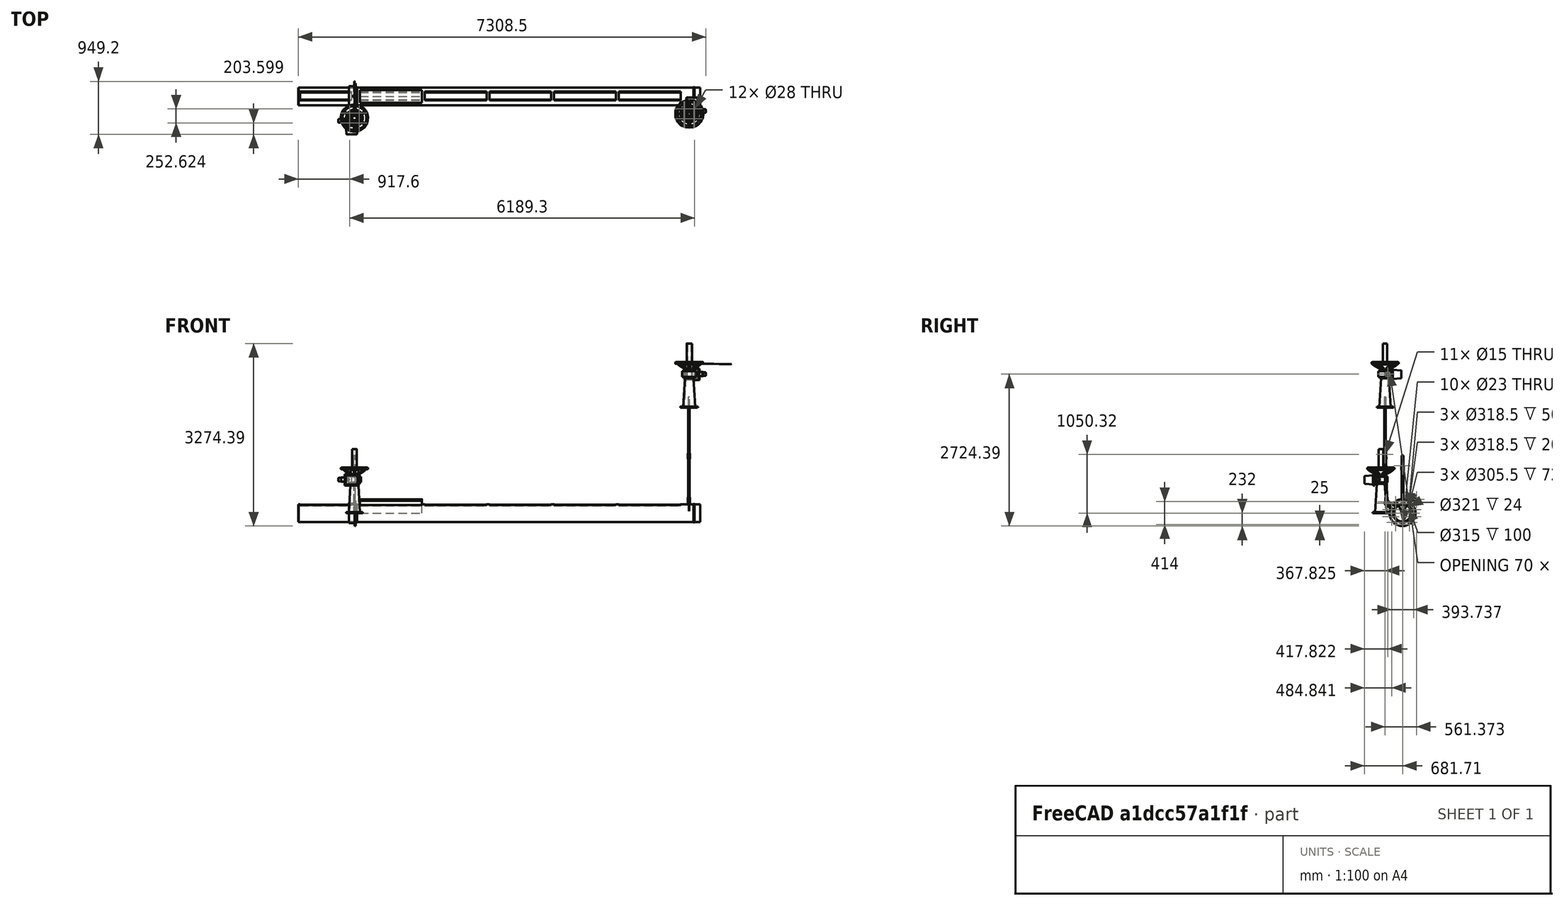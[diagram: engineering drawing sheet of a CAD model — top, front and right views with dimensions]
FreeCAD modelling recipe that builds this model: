
FCSTD DOCUMENT  (FreeCAD 0.21R33771 (Git))
Label: pipeSkimmer2
License: All rights reserved
LicenseURL: https://en.wikipedia.org/wiki/All_rights_reserved
objects: Part::Extrusion×9, Sketcher::SketchObject×9, App::FeaturePython×8, Part::FeaturePython×7, App::Part×7, Part::Compound×4, Part::Cut×3, Part::Revolution×1, Spreadsheet::Sheet×1, Part::Feature×1, Part::Cylinder×1
note: 34 computed .brp shape members not serialized (recipe doc carries the construction recipe); baked Part::Feature solids carry a one-line shape summary decoded from their .brp

FEATURE [Part::FeaturePython] Flange  # WARN: FeaturePython — macro-defined, semantics opaque (R4)
  Placement = pos=(0,0,0) rot=(0.57735,0.57735,0.57735;2.0944rad)
  dia = 6
  fittings = 00_Flange
  material = 0
  standard = 1
FEATURE [Part::FeaturePython] Ring  # WARN: FeaturePython — macro-defined, semantics opaque (R4)
  D = 360
  Placement = pos=(0,0,0) rot=(0,1,0;1.5708rad)
  d = 315
  sface = 0
FEATURE [Part::Extrusion] Extrude
  Base = -> Ring
  Dir = (1,0,0)
  DirMode = 2
  FaceMakerClass = Part::FaceMakerBullseye
  LengthFwd = 100
  LengthRev = 0
  Reversed = true
  Solid = true
  Symmetric = false
FEATURE [App::Part] Part  label="brg01"
  Group = -> [Ring,Extrude,Flange]
  Origin = -> Origin
  Placement = pos=(6200,-1.1983e-12,0) rot=(0,0,1;0rad)
  expr: .Placement.Base.x = Spreadsheet.L0 - Spreadsheet.l1 + Spreadsheet.l1 - 300
FEATURE [Part::FeaturePython] Straight_tube  # WARN: FeaturePython — macro-defined, semantics opaque (R4)
  L = 7200
  Placement = pos=(-1000,0,0) rot=(0,0,1;0rad)
  dia = 16
  fittings = 05_Straight pipe
  material = 1
  standard = 1
  expr: .Placement.Base.x = -Spreadsheet.l1
  expr: L = Spreadsheet.L0 + Spreadsheet.l1 - 300
FEATURE [Sketcher::SketchObject] Sketch
  FullyConstrained = true
  Placement = pos=(0,0,0) rot=(1,0,0;1.5708rad)
  expr: Constraints[35] = Spreadsheet.L0 - 400
  sketch-geometry (12):
    g0: LineSegment StartX=6080 StartY=159.25 StartZ=0 EndX=6100 EndY=159.25 EndZ=0
    g1: LineSegment StartX=6100 StartY=159.25 StartZ=0 EndX=6100 EndY=164.25 EndZ=0
    g2: LineSegment StartX=6100 StartY=164.25 StartZ=0 EndX=6080 EndY=164.25 EndZ=0
    g3: LineSegment StartX=6080 StartY=164.25 StartZ=0 EndX=6080 EndY=159.25 EndZ=0
    g4: LineSegment StartX=0 StartY=159.25 StartZ=0 EndX=0 EndY=169.25 EndZ=0
    g5: LineSegment StartX=0 StartY=169.25 StartZ=0 EndX=19 EndY=169.25 EndZ=0
    g6: LineSegment StartX=19 StartY=169.25 StartZ=0 EndX=19 EndY=164.25 EndZ=0
    g7: LineSegment StartX=19 StartY=164.25 StartZ=0 EndX=31 EndY=164.25 EndZ=0
    g8: LineSegment StartX=31 StartY=164.25 StartZ=0 EndX=31 EndY=169.25 EndZ=0
    g9: LineSegment StartX=31 StartY=169.25 StartZ=0 EndX=50 EndY=169.25 EndZ=0
    g10: LineSegment StartX=50 StartY=169.25 StartZ=0 EndX=50 EndY=159.25 EndZ=0
    g11: LineSegment StartX=50 StartY=159.25 StartZ=0 EndX=0 EndY=159.25 EndZ=0
  constraints (36):
    c: Coincident(g0,g1)
    c: Coincident(g1,g2)
    c: Coincident(g2,g3)
    c: Coincident(g3,g0)
    c: Horizontal(g0)
    c: Horizontal(g2)
    c: Vertical(g1)
    c: Vertical(g3)
    c: DistanceY(g-1,g0) = 159.25
    c: DistanceY(g1,g1) = 5
    c: DistanceX(g2,g2) = 20
    c: Vertical(g4)
    c: Coincident(g4,g5)
    c: Horizontal(g5)
    c: Coincident(g5,g6)
    c: Vertical(g6)
    c: Coincident(g6,g7)
    c: Coincident(g7,g8)
    c: Coincident(g8,g9)
    c: Coincident(g9,g10)
    c: Coincident(g10,g11)
    c: Coincident(g11,g4)
    c: Horizontal(g11)
    c: Vertical(g10)
    c: Horizontal(g7)
    c: Horizontal(g9)
    c: Vertical(g8)
    c: DistanceY(g10,g10) = 10
    c: DistanceY(g7,g8) = 5
    c: Horizontal(g8,g5)
    c: DistanceX(g11,g11) = 50
    c: DistanceX(g7,g7) = 12
    c: DistanceX(g5,g5) = 19
    c: DistanceY(g-1,g4) = 159.25
    c: Vertical(g-1,g4)
    c: DistanceX(g-1,g0) = 6100
FEATURE [Part::Revolution] Revolve
  Angle = 360
  Axis = (1,0,0)
  Base = (0,0,0)
  FaceMakerClass = Part::FaceMakerBullseye
  Solid = true
  Source = -> Sketch
  Symmetric = false
FEATURE [Spreadsheet::Sheet] Spreadsheet  label="Spreadsheet_pipeSkimmer"
  cells = A2='tankDia  D0; B2(D0)=13000; A3='fullLength L0; B3(L0)=6500; A4='length       l1; B4(l1)=1000; A5='越流堰数 n0; B5(n0)=5; A6='越流堰長 l3; B6(l3)=1110; A7='開閉台  h2; B7(h2)=1500; A8='開閉台 位置 l2; B8(l2)=500
FEATURE [Sketcher::SketchObject] Sketch001
  FullyConstrained = false
  Placement = pos=(0,0,0) rot=(0.57735,0.57735,0.57735;2.0944rad)
  sketch-geometry (3):
    g0: LineSegment StartX=0 StartY=0 StartZ=0 EndX=114.659 EndY=220.257 EndZ=0
    g1: LineSegment StartX=0 StartY=0 StartZ=0 EndX=-114.659 EndY=220.257 EndZ=0
    g2: ArcOfCircle CenterX=0 CenterY=0 CenterZ=0 NormalX=0 NormalY=0 NormalZ=1 AngleXU=0 Radius=248.314 StartAngle=1.09083 EndAngle=2.05076
  constraints (7):
    c: Coincident(g-1,g0)
    c: Coincident(g1,g0)
    c: Coincident(g2,g0)
    c: Coincident(g2,g1)
    c: Coincident(g2,g0)
    c: Angle(g0,g-2) = 0.479966
    c: Angle(g0,g1) = 0.959931
FEATURE [Part::Extrusion] Extrude001
  Base = -> Sketch001
  Dir = (1,0,0)
  DirMode = 2
  FaceMakerClass = Part::FaceMakerBullseye
  LengthFwd = 1110
  LengthRev = 0
  Placement = pos=(100,0,0) rot=(0,0,1;0rad)
  Solid = true
  Symmetric = false
  expr: LengthFwd = Spreadsheet.l3
FEATURE [Part::FeaturePython] Array  # Draft array (typed FeaturePython)
  AlwaysSyncPlacement = false
  Angle = 360
  ArrayType = 0
  Axis = (0,0,1)
  Base = -> Extrude001
  Center = (0,0,0)
  Count = 5
  ExpandArray = false
  Fuse = false
  IntervalAxis = (0,0,0)
  IntervalX = (1160,0,0)
  IntervalY = (0,100,0)
  IntervalZ = (0,0,100)
  NumberCircles = 3
  NumberPolar = 5
  NumberX = 5
  NumberY = 1
  NumberZ = 1
  PlacementList = 5 placements: arithmetic series from (100,0,0) step (1160,0,0) to (4740,0,0)
  RadialDistance = 50
  ScaleList = (5) [(1,1,1),(1,1,1),(1,1,1),(1,1,1),(1,1,1)]
  Symmetry = 1
  TangentialDistance = 25
  expr: .IntervalX.x = Spreadsheet.l3 + 50
  expr: NumberX = Spreadsheet.n0
FEATURE [Part::Cut] Cut
  Base = -> Straight_tube
  Tool = -> Array
FEATURE [Sketcher::SketchObject] Sketch002
  FullyConstrained = false
  Placement = pos=(-30,0,0) rot=(0.57735,0.57735,0.57735;2.0944rad)
  expr: .Placement.Base.x = -30
  sketch-geometry (3):
    g0: LineSegment StartX=0 StartY=0 StartZ=0 EndX=-124.513 EndY=239.188 EndZ=0
    g1: LineSegment StartX=0 StartY=0 StartZ=0 EndX=124.513 EndY=239.188 EndZ=0
    g2: ArcOfCircle CenterX=0 CenterY=0 CenterZ=0 NormalX=0 NormalY=0 NormalZ=1 AngleXU=0 Radius=269.656 StartAngle=1.09083 EndAngle=2.05076
  constraints (7):
    c: Coincident(g0,g-1)
    c: Coincident(g1,g0)
    c: Coincident(g2,g1)
    c: Coincident(g2,g0)
    c: Coincident(g2,g0)
    c: Angle(g1,g0) = 0.959931
    c: Angle(g1,g-2) = 0.479966
FEATURE [Part::Extrusion] Extrude002
  Base = -> Sketch002
  Dir = (1,0,0)
  DirMode = 2
  FaceMakerClass = Part::FaceMakerBullseye
  LengthFwd = 920
  LengthRev = 0
  Placement = pos=(-25,0,0) rot=(0,0,1;0rad)
  Reversed = true
  Solid = true
  Symmetric = false
  expr: LengthFwd = Spreadsheet.l1 - 80
FEATURE [Part::Cut] Cut001
  Base = -> Cut
  Tool = -> Extrude002
FEATURE [Sketcher::SketchObject] Sketch004
  FullyConstrained = true
  Placement = pos=(0,0,0) rot=(0.57735,0.57735,0.57735;2.0944rad)
  sketch-geometry (6):
    g0: LineSegment StartX=0 StartY=0 StartZ=0 EndX=247.487 EndY=247.487 EndZ=0
    g1: Circle CenterX=247.487 CenterY=247.487 CenterZ=0 NormalX=0 NormalY=0 NormalZ=1 AngleXU=0 Radius=7.5
    g2: ArcOfCircle CenterX=247.487 CenterY=247.487 CenterZ=0 NormalX=0 NormalY=0 NormalZ=1 AngleXU=0 Radius=20 StartAngle=5.62869 EndAngle=8.50848
    g3: LineSegment StartX=235.312 StartY=263.354 StartZ=0 EndX=74.8903 EndY=140.258 EndZ=0
    g4: LineSegment StartX=263.354 StartY=235.312 StartZ=0 EndX=140.258 EndY=74.8903 EndZ=0
    g5: ArcOfCircle CenterX=0 CenterY=0 CenterZ=0 NormalX=0 NormalY=0 NormalZ=1 AngleXU=0 Radius=159 StartAngle=0.490434 EndAngle=1.08036
  constraints (15):
    c: Coincident(g0,g-1)
    c: Angle(g-1,g0) = 0.785398
    c: Coincident(g1,g0)
    c: Radius(g1) = 7.5
    c: Coincident(g2,g1)
    c: Coincident(g5,g3)
    c: Coincident(g5,g4)
    c: Coincident(g5,g0)
    c: Tangent(g2,g3) = -1.5708
    c: Tangent(g2,g4) = 1.5708
    c: Equal(g4,g3)
    c: Radius(g5) = 159
    c: Angle(g3,g4) = 0.261799
    c: Distance(g5,g1) = 350
    c: Radius(g2) = 20
FEATURE [Part::Extrusion] Extrude004
  Base = -> Sketch004
  Dir = (1,0,0)
  DirMode = 2
  FaceMakerClass = Part::FaceMakerBullseye
  LengthFwd = 6
  LengthRev = 0
  Solid = true
  Symmetric = true
FEATURE [App::Part] Part003  label="arm"
  Group = -> [Sketch004,Extrude004]
  Origin = -> Origin003
  Placement = pos=(6000,0,0) rot=(1,0,0;1.8326rad)
  expr: .Placement.Base.x = Spreadsheet.L0 - Spreadsheet.l2
FEATURE [Sketcher::SketchObject] Sketch005
  ExternalGeometry = -> [Cut001]
  FullyConstrained = true
  MapMode = 5
  Placement = pos=(-1000,0,0) rot=(0.57735,-0.57735,-0.57735;2.0944rad)
  expr: .Placement.Base.x = -Spreadsheet.l1
  sketch-geometry (1):
    g0: Circle CenterX=0 CenterY=0 CenterZ=0 NormalX=0 NormalY=0 NormalZ=1 AngleXU=0 Radius=159.25
  constraints (2):
    c: Coincident(g0,g-1)
    c: Equal(g0,g-3)
FEATURE [Part::Extrusion] Extrude005
  Base = -> Sketch005
  Dir = (-1,0,0)
  DirMode = 2
  FaceMakerClass = Part::FaceMakerBullseye
  LengthFwd = 6
  LengthRev = 0
  Solid = true
  Symmetric = false
FEATURE [App::Part] Part001  label="pipe"
  Group = -> [Sketch,Revolve,Cut,Cut001,Sketch002,Sketch001,Straight_tube,Array,Extrude002,Extrude001,Sketch005,Extrude005,Part003]
  Origin = -> Origin001
FEATURE [Part::Feature] Part__Feature  label="電動トップハンドル_LTKD-01 v5"
  Placement = pos=(0,-389.711,-5.7e-14) rot=(1,0,0;1.5708rad)
  shape: bbox 555.2 x 557.2 x 1150 mm, 73 faces (baked)
FEATURE [App::Part] Part004  label="開閉台"
  Group = -> [Part__Feature]
  Origin = -> Origin004
  Placement = pos=(0,-400,1500) rot=(0,0,1;3.14159rad)
  expr: .Placement.Base.z = Spreadsheet.h2
FEATURE [Sketcher::SketchObject] Sketch006
  FullyConstrained = false
  Placement = pos=(0,0,0) rot=(0.57735,0.57735,0.57735;2.0944rad)
  sketch-geometry (5):
    g0: Circle CenterX=0 CenterY=0 CenterZ=0 NormalX=0 NormalY=0 NormalZ=1 AngleXU=0 Radius=7.5
    g1: ArcOfCircle CenterX=0 CenterY=0 CenterZ=0 NormalX=0 NormalY=0 NormalZ=1 AngleXU=0 Radius=20 StartAngle=3.14159 EndAngle=6.28319
    g2: LineSegment StartX=-20 StartY=9.32106e-06 StartZ=0 EndX=-20 EndY=80 EndZ=0
    g3: LineSegment StartX=-20 StartY=80 StartZ=0 EndX=20 EndY=80 EndZ=0
    g4: LineSegment StartX=20 StartY=80 StartZ=0 EndX=20 EndY=3.56439e-05 EndZ=0
  constraints (13):
    c: Coincident(g0,g-1)
    c: Coincident(g1,g0)
    c: Radius(g1) = 20
    c: Radius(g0) = 7.5
    c: Vertical(g2)
    c: Coincident(g2,g3)
    c: Horizontal(g3)
    c: Coincident(g3,g4)
    c: Vertical(g4)
    c: Coincident(g1,g4)
    c: Coincident(g1,g2)
    c: DistanceY(g-1,g3) = 80
    c: DistanceX(g3,g3) = 40
FEATURE [Part::Extrusion] Extrude006
  Base = -> Sketch006
  Dir = (1,0,0)
  DirMode = 2
  FaceMakerClass = Part::FaceMakerBullseye
  LengthFwd = 40
  LengthRev = 0
  Solid = true
  Symmetric = true
FEATURE [Sketcher::SketchObject] Sketch007
  ExternalGeometry = -> [Extrude006]
  FullyConstrained = false
  MapMode = 5
  Placement = pos=(0,-20,0) rot=(1,0,0;1.5708rad)
  sketch-geometry (4):
    g0: LineSegment StartX=-5 StartY=-25.0355 StartZ=0 EndX=5 EndY=-25.0355 EndZ=0
    g1: LineSegment StartX=5 StartY=-25.0355 StartZ=0 EndX=5 EndY=60 EndZ=0
    g2: LineSegment StartX=5 StartY=60 StartZ=0 EndX=-5 EndY=60 EndZ=0
    g3: LineSegment StartX=-5 StartY=60 StartZ=0 EndX=-5 EndY=-25.0355 EndZ=0
  constraints (11):
    c: Coincident(g0,g1)
    c: Coincident(g1,g2)
    c: Coincident(g2,g3)
    c: Coincident(g3,g0)
    c: Horizontal(g0)
    c: Horizontal(g2)
    c: Vertical(g1)
    c: Vertical(g3)
    c: Distance(g1,g-3) = 20
    c: DistanceX(g0,g0) = 10
    c: DistanceX(g0,g-1) = 5
FEATURE [Part::Extrusion] Extrude007
  Base = -> Sketch007
  Dir = (0,-1,2e-16)
  DirMode = 2
  FaceMakerClass = Part::FaceMakerBullseye
  LengthFwd = 50
  LengthRev = 0
  Reversed = true
  Solid = true
  Symmetric = false
FEATURE [Part::Cut] Cut002
  Base = -> Extrude006
  Tool = -> Extrude007
FEATURE [Sketcher::SketchObject] Sketch008
  FullyConstrained = true
  MapMode = 5
  Placement = pos=(0,0,80) rot=(0,0,1;0rad)
  sketch-geometry (1):
    g0: Circle CenterX=0 CenterY=0 CenterZ=0 NormalX=0 NormalY=0 NormalZ=1 AngleXU=0 Radius=15
  constraints (2):
    c: Coincident(g0,g-1)
    c: Radius(g0) = 15
FEATURE [Part::Extrusion] Extrude008
  Base = -> Sketch008
  Dir = (0,0,1)
  DirMode = 2
  FaceMakerClass = Part::FaceMakerBullseye
  LengthFwd = 700
  LengthRev = 0
  Solid = true
  Symmetric = false
FEATURE [Part::FeaturePython] Clone  label="Cut003"  # Draft clone (typed FeaturePython)
  AttacherType = Attacher::AttachEngine3D
  Fuse = false
  Objects = -> [Cut002]
  Placement = pos=(-1.83e-13,0,850) rot=(0,1,0;3.14159rad)
  Scale = (1,1,1)
FEATURE [App::Part] Part005  label="rod"
  Group = -> [Cut002,Clone,Sketch007,Sketch006,Sketch008,Extrude006,Extrude007,Extrude008]
  Origin = -> Origin005
FEATURE [Part::Compound] Compound001  label="pipe001"
  Links = -> [Part001]
FEATURE [Sketcher::SketchObject] Sketch009
  FullyConstrained = false
  Placement = pos=(0,0,0) rot=(0.57735,0.57735,0.57735;2.0944rad)
  sketch-geometry (5):
    g0: Circle CenterX=0 CenterY=0 CenterZ=0 NormalX=0 NormalY=0 NormalZ=1 AngleXU=0 Radius=7.5
    g1: ArcOfCircle CenterX=0 CenterY=0 CenterZ=0 NormalX=0 NormalY=0 NormalZ=1 AngleXU=0 Radius=20 StartAngle=3.14864 EndAngle=6.2925
    g2: LineSegment StartX=-19.9995 StartY=-0.141043 StartZ=0 EndX=-19.9995 EndY=80 EndZ=0
    g3: LineSegment StartX=-19.9995 StartY=80 StartZ=0 EndX=19.9991 EndY=80 EndZ=0
    g4: LineSegment StartX=19.9991 StartY=80 StartZ=0 EndX=19.9991 EndY=0.186233 EndZ=0
  constraints (12):
    c: Coincident(g0,g-1)
    c: Coincident(g1,g0)
    c: Vertical(g2)
    c: Coincident(g2,g3)
    c: Horizontal(g3)
    c: Coincident(g3,g4)
    c: Vertical(g4)
    c: Coincident(g1,g4)
    c: Coincident(g1,g2)
    c: Radius(g0) = 7.5
    c: Radius(g1) = 20
    c: DistanceY(g-1,g3) = 80
FEATURE [Part::Extrusion] Extrude009
  Base = -> Sketch009
  Dir = (1,0,0)
  DirMode = 2
  FaceMakerClass = Part::FaceMakerBullseye
  LengthFwd = 9
  LengthRev = 0
  Solid = true
  Symmetric = true
FEATURE [Part::Cylinder] Cylinder  label="円柱"
  Angle = 360
  AttacherType = Attacher::AttachEngine3D
  FirstAngle = 0
  Height = 1000
  Placement = pos=(0,0,30) rot=(0,0,1;0rad)
  Radius = 15
  SecondAngle = 0
FEATURE [App::Part] Part006  label="rod002"
  Group = -> [Sketch009,Cylinder,Extrude009]
  Origin = -> Origin006
FEATURE [Part::Compound] Compound002  label="rod003"
  Links = -> [Part006]
  Placement = pos=(5997.5,-313.885,1050.32) rot=(0.999862,-0.016587,0.000261;2e-06rad)
  expr: .Placement.Base.x = Spreadsheet.L0 - Spreadsheet.l2
FEATURE [Part::Compound] Compound003  label="開閉台001"
  Links = -> [Part004]
  Placement = pos=(6012.5,-303.595,392.389) rot=(0.999893,-0.016586,0;2e-06rad)
  expr: .Placement.Base.x = Spreadsheet.L0 - Spreadsheet.l2
FEATURE [Part::Compound] Compound
  Links = -> [Part005]
  Placement = pos=(5998,-286.703,200.752) rot=(1,-1e-06,0;0.031984rad)
  expr: .Placement.Base.x = Spreadsheet.L0 - Spreadsheet.l2
FEATURE [Part::FeaturePython] pipe001_001  label="pipeA"  # a2plus imported part (geometry in sourceFile) (typed FeaturePython)
  Placement = pos=(0,0,0) rot=(1,0,0;-0.087266rad)
  a2p_Version = 0.4.67
  fixedPosition = true
  localSourceObject = Compound001
  objectType = a2pPart
  sourceFile = converted
  subassemblyImport = false
  timeLastImport = 1.72786e+09
  updateColors = true
FEATURE [App::FeaturePython] circularEdge_001  label="circularEdge_001__Compound"  # a2plus constraint (typed FeaturePython)
  Object1 = pipe001_001
  Object2 = Compound
  ParentTreeObject = -> pipe001_001
  SubElement1 = Edge139
  SubElement2 = Edge26
  Suppressed = false
  Type = circularEdge
  directionConstraint = 1
  lockRotation = false
  offset = 0
FEATURE [App::FeaturePython] circularEdge_001_mirror  label="circularEdge_001__pipeA"  # a2plus constraint (typed FeaturePython)
  Object1 = pipe001_001
  Object2 = Compound
  ParentTreeObject = -> Compound
  SubElement1 = Edge139
  SubElement2 = Edge26
  Suppressed = false
  Type = circularEdge
  directionConstraint = 1
  lockRotation = false
  offset = 0
FEATURE [App::FeaturePython] circularEdge_002  label="circularEdge_002__Compound"  # a2plus constraint (typed FeaturePython)
  Object1 = Compound002
  Object2 = Compound
  ParentTreeObject = -> Compound002
  SubElement1 = Edge6
  SubElement2 = Edge56
  Suppressed = false
  Type = circularEdge
  directionConstraint = 0
  lockRotation = false
  offset = 0
FEATURE [App::FeaturePython] circularEdge_002_mirror  label="circularEdge_002__rod003"  # a2plus constraint (typed FeaturePython)
  Object1 = Compound002
  Object2 = Compound
  ParentTreeObject = -> Compound
  SubElement1 = Edge6
  SubElement2 = Edge56
  Suppressed = false
  Type = circularEdge
  directionConstraint = 0
  lockRotation = false
  offset = 0
FEATURE [App::FeaturePython] axisCoincident_001  label="axisCoincident_001__開閉台001"  # a2plus constraint (typed FeaturePython)
  Object1 = Compound002
  Object2 = Compound003
  ParentTreeObject = -> Compound002
  SubElement1 = Edge1
  SubElement2 = Face72
  Suppressed = false
  Type = axial
  directionConstraint = 1
  lockRotation = false
FEATURE [App::FeaturePython] axisCoincident_001_mirror  label="axisCoincident_001__rod003"  # a2plus constraint (typed FeaturePython)
  Object1 = Compound002
  Object2 = Compound003
  ParentTreeObject = -> Compound003
  SubElement1 = Edge1
  SubElement2 = Face72
  Suppressed = false
  Type = axial
  directionConstraint = 1
  lockRotation = false
FEATURE [Part::FeaturePython] _________001_001  label="開閉台001_001"  # a2plus imported part (geometry in sourceFile) (typed FeaturePython)
  Placement = pos=(-2.49999,16.4058,-0.000428049) rot=(0,0,1;0rad)
  a2p_Version = 0.4.67
  fixedPosition = false
  localSourceObject = Compound003
  objectType = a2pPart
  sourceFile = converted
  subassemblyImport = false
  timeLastImport = 1.72786e+09
  updateColors = true
FEATURE [App::FeaturePython] axisCoincident_002  label="axisCoincident_002__開閉台001_001"  # a2plus constraint (typed FeaturePython)
  Object1 = Compound002
  Object2 = _________001_001
  ParentTreeObject = -> Compound002
  SubElement1 = Face1
  SubElement2 = Face72
  Suppressed = false
  Type = axial
  directionConstraint = 0
  lockRotation = false
FEATURE [App::Part] Part002  label="pipeSkimmer"
  Group = -> [Part001,Part,Spreadsheet,Part004,Part005,Compound001,Part006,Compound002,Compound003,Compound,pipe001_001,circularEdge_002_mirror,circularEdge_001_mirror,circularEdge_002,axisCoincident_001,axisCoincident_001_mirror,_________001_001,axisCoincident_002]
  Origin = -> Origin002
FEATURE [App::FeaturePython] axisCoincident_002_mirror  label="axisCoincident_002__rod003"  # a2plus constraint (typed FeaturePython)
  Object1 = Compound002
  Object2 = _________001_001
  ParentTreeObject = -> _________001_001
  SubElement1 = Face1
  SubElement2 = Face72
  Suppressed = false
  Type = axial
  directionConstraint = 0
  lockRotation = false
